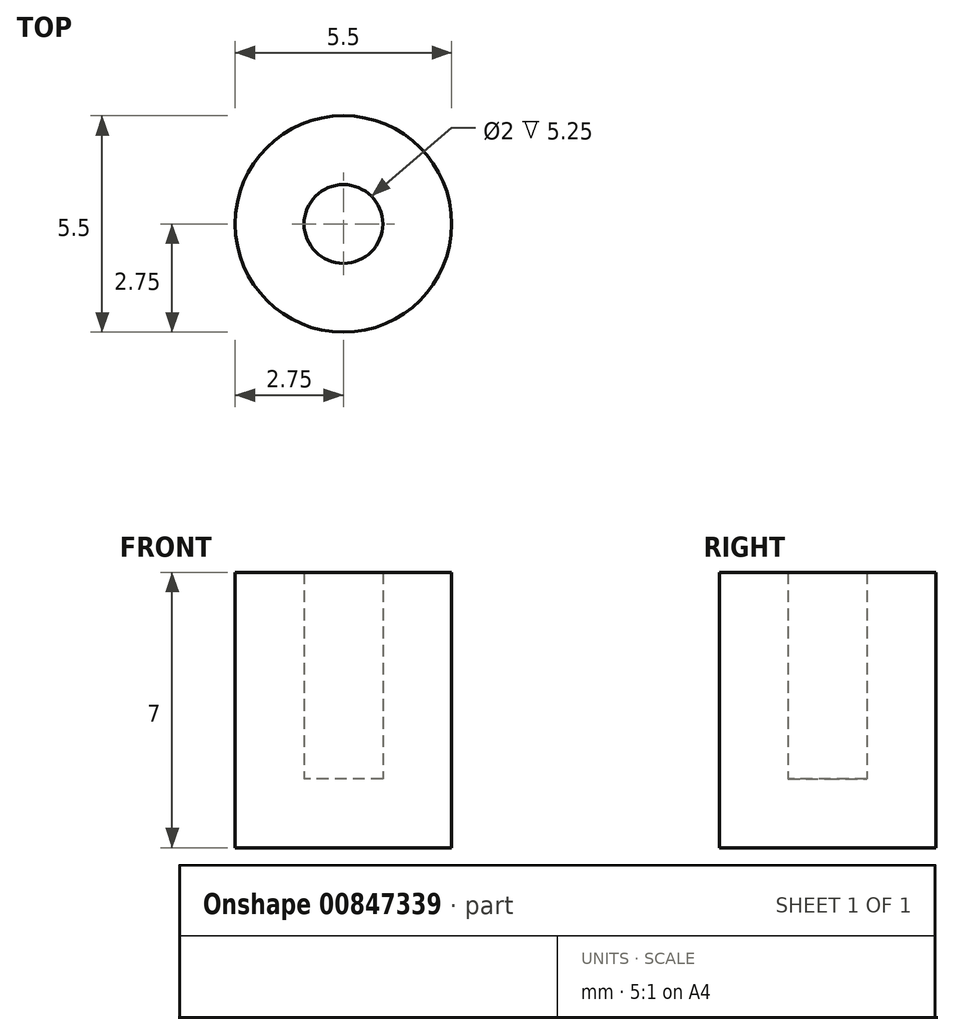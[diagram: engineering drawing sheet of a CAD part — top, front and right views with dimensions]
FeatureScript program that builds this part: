
annotation { "Feature Type Name" : "Feature", "Feature Type Description" : "" }
export const myFeature = defineFeature(function(context is Context, id is Id, definition is map)
    precondition{}
    {
        {
            var Q0;
            Q0=qCreatedBy(makeId("Top.planeOp"),FACE);
            var sketch = newSketch(context, id + "F0", { "sketchPlane" : qUnion([Q0])});
            skCircle(sketch, "E0", {"center": v(0, 0) * mm, "radius": 2.75 * mm});
            skSolve(sketch);
        }
        {
            var Q0;
            Q0 = qSketchRegion(id + "F0", true);
            var Q1;
            Q1=sQuery(id+"F0.wireOp",EDGE,"E0");
            extrude(context, id + "F1", {"entities" : qUnion([Q0]), "surfaceEntities" : qUnion([Q1]), "depth" : 7 * mm, "offsetDistance" : 25 * mm});
        }
        {
            var Q0;
            Q0=makeQuery(id+"F1.opExtrude","CAP_FACE",FACE,{"disambiguationData":[OSD([sQuery(id+"F0.wireOp",EDGE,"E0")])],"isStart":false});
            shell(context, id + "F2", {"entities" : qUnion([Q0]), "thickness" : 1.75 * mm});
        }
    });
